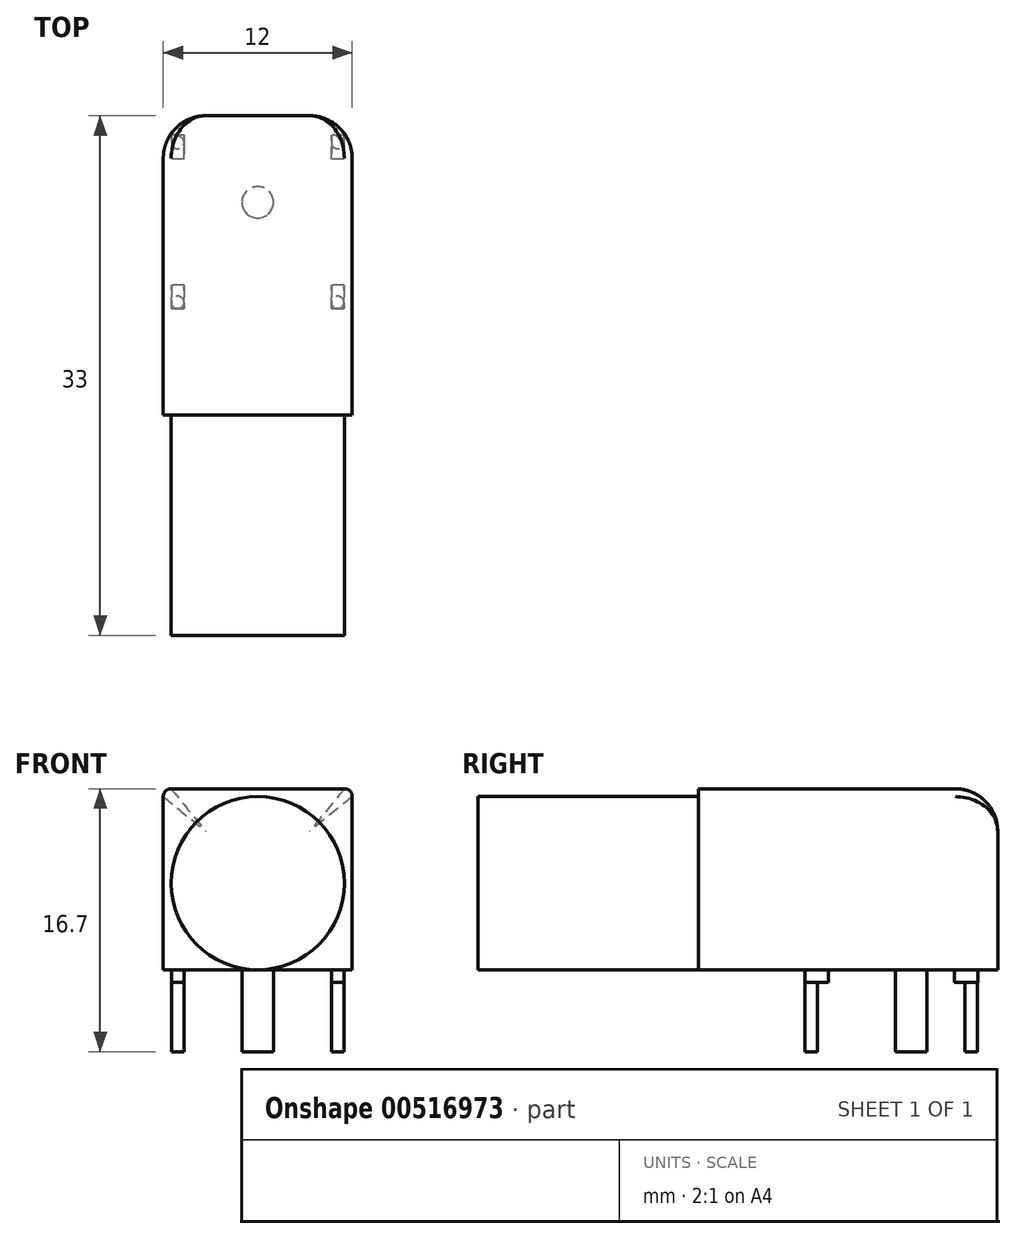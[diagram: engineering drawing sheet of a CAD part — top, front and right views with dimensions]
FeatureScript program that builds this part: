
annotation { "Feature Type Name" : "Feature", "Feature Type Description" : "" }
export const myFeature = defineFeature(function(context is Context, id is Id, definition is map)
    precondition{}
    {
        {
            var Q0;
            Q0=qCreatedBy(makeId("Front.planeOp"),FACE);
            var sketch = newSketch(context, id + "F0", { "sketchPlane" : qUnion([Q0])});
            skLineSegment(sketch, "E0.bottom", {"start": v(-6, 6) * mm, "end": v(6, 6) * mm});
            skLineSegment(sketch, "E0.top", {"start": v(-6, -5.5) * mm, "end": v(6, -5.5) * mm});
            skLineSegment(sketch, "E0.left", {"start": v(-6, 6) * mm, "end": v(-6, -5.5) * mm});
            skLineSegment(sketch, "E0.right", {"start": v(6, 6) * mm, "end": v(6, -5.5) * mm});
            skSolve(sketch);
        }
        {
            var Q0;
            Q0 = qSketchRegion(id + "F0", true);
            extrude(context, id + "F1", {"entities" : qUnion([Q0]), "oppositeDirection" : true, "depth" : 19 * mm, "offsetDistance" : 25 * mm});
        }
        {
            var Q0;
            Q0=qCreatedBy(makeId("Front.planeOp"),FACE);
            var sketch = newSketch(context, id + "F2", { "sketchPlane" : qUnion([Q0])});
            skCircle(sketch, "E1", {"center": v(0, 0) * mm, "radius": 5.5 * mm});
            skSolve(sketch);
        }
        {
            var Q0;
            Q0 = qSketchRegion(id + "F2", true);
            extrude(context, id + "F3", {"entities" : qUnion([Q0]), "operationType" : NewBodyOperationType.ADD, "depth" : 14 * mm, "offsetDistance" : 25 * mm});
        }
        {
            var Q0;
            Q0=makeQuery(id+"F1.opExtrude","SWEPT_EDGE",EDGE,{"disambiguationData":[OSD([sQuery(id+"F0.wireOp",EDGE,"E0.bottom"),sQuery(id+"F0.wireOp",EDGE,"E0.right")])]});
            var Q1;
            Q1=makeQuery(id+"F1.opExtrude","SWEPT_EDGE",EDGE,{"disambiguationData":[OSD([sQuery(id+"F0.wireOp",EDGE,"E0.bottom"),sQuery(id+"F0.wireOp",EDGE,"E0.left")])]});
            fillet(context, id + "F4", {"entities" : qUnion([Q0, Q1]), "radius" : 0.5 * mm, "tangentPropagation" : true, "allowEdgeOverflow" : false});
        }
        {
            var Q0;
            Q0=makeQuery(id+"F1.opExtrude","CAP_EDGE",EDGE,{"disambiguationData":[OSD([sQuery(id+"F0.wireOp",EDGE,"E0.bottom")])],"isStart":false});
            fillet(context, id + "F5", {"entities" : qUnion([Q0]), "radius" : 2.7 * mm, "tangentPropagation" : true, "allowEdgeOverflow" : false});
        }
        {
            var Q0;
            Q0=qCreatedBy(makeId("Top.planeOp"),FACE);
            var sketch = newSketch(context, id + "F6", { "sketchPlane" : qUnion([Q0])});
            skCircle(sketch, "E2", {"center": v(0, 13.5) * mm, "radius": 1 * mm});
            skCircle(sketch, "E3", {"center": v(-5.08, 7.14) * mm, "radius": 0.4 * mm});
            skCircle(sketch, "E4", {"center": v(5.08, 7.14) * mm, "radius": 0.4 * mm});
            skCircle(sketch, "E5", {"center": v(-5.08, 17.3) * mm, "radius": 0.4 * mm});
            skCircle(sketch, "E6", {"center": v(5.08, 17.3) * mm, "radius": 0.4 * mm});
            skSolve(sketch);
        }
        {
            var Q0;
            Q0 = qSketchRegion(id + "F6", true);
            extrude(context, id + "F7", {"entities" : qUnion([Q0]), "operationType" : NewBodyOperationType.ADD, "oppositeDirection" : true, "depth" : 10.7 * mm, "offsetDistance" : 25 * mm});
        }
        {
            var Q0;
            Q0=qCreatedBy(makeId("Top.planeOp"),FACE);
            var sketch = newSketch(context, id + "F8", { "sketchPlane" : qUnion([Q0])});
            skLineSegment(sketch, "E7.bottom", {"start": v(-5.48, 8.24) * mm, "end": v(-4.68, 8.24) * mm});
            skLineSegment(sketch, "E7.top", {"start": v(-5.48, 6.74) * mm, "end": v(-4.68, 6.74) * mm});
            skLineSegment(sketch, "E7.left", {"start": v(-5.48, 8.24) * mm, "end": v(-5.48, 6.74) * mm});
            skLineSegment(sketch, "E7.right", {"start": v(-4.68, 8.24) * mm, "end": v(-4.68, 6.74) * mm});
            skLineSegment(sketch, "E8.bottom", {"start": v(4.68, 8.24) * mm, "end": v(5.48, 8.24) * mm});
            skLineSegment(sketch, "E8.top", {"start": v(4.68, 6.74) * mm, "end": v(5.48, 6.74) * mm});
            skLineSegment(sketch, "E8.left", {"start": v(4.68, 8.24) * mm, "end": v(4.68, 6.74) * mm});
            skLineSegment(sketch, "E8.right", {"start": v(5.48, 8.24) * mm, "end": v(5.48, 6.74) * mm});
            skLineSegment(sketch, "E9.bottom", {"start": v(-5.48, 17.75) * mm, "end": v(-4.68, 17.75) * mm});
            skLineSegment(sketch, "E9.top", {"start": v(-5.48, 16.25) * mm, "end": v(-4.68, 16.25) * mm});
            skLineSegment(sketch, "E9.left", {"start": v(-5.48, 17.75) * mm, "end": v(-5.48, 16.25) * mm});
            skLineSegment(sketch, "E9.right", {"start": v(-4.68, 17.75) * mm, "end": v(-4.68, 16.25) * mm});
            skLineSegment(sketch, "E10.bottom", {"start": v(4.68, 17.75) * mm, "end": v(5.48, 17.75) * mm});
            skLineSegment(sketch, "E10.top", {"start": v(4.68, 16.25) * mm, "end": v(5.48, 16.25) * mm});
            skLineSegment(sketch, "E10.left", {"start": v(4.68, 17.75) * mm, "end": v(4.68, 16.25) * mm});
            skLineSegment(sketch, "E10.right", {"start": v(5.48, 17.75) * mm, "end": v(5.48, 16.25) * mm});
            skSolve(sketch);
        }
        {
            var Q0;
            Q0 = qSketchRegion(id + "F8", true);
            extrude(context, id + "F9", {"entities" : qUnion([Q0]), "operationType" : NewBodyOperationType.ADD, "oppositeDirection" : true, "depth" : 6.3 * mm, "offsetDistance" : 25 * mm});
        }
    });
